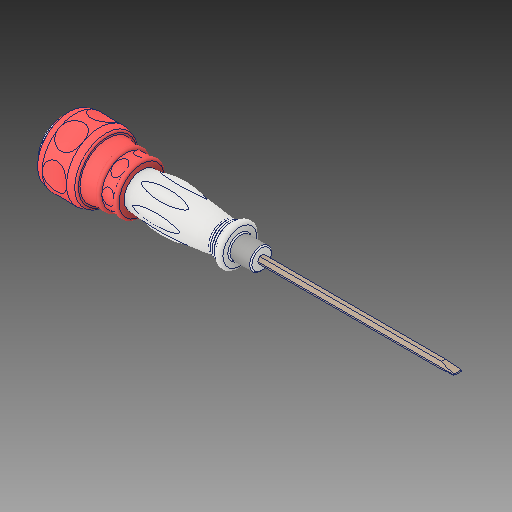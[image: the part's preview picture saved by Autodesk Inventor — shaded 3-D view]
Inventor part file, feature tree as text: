
AUTODESK INVENTOR PART (.ipt)
format: ipt  version: 2018 (Build 220112000, 112)  size: 310,784 bytes
history: native  units: in
note: dims shown in document units (in); Inventor stores cm internally (conversion verified against a paired STEP export)
features: fillet x1
ambient origin geometry x8: Origin, YZ Plane, XZ Plane, XY Plane, X Axis, Y Axis, Z Axis, Center Point
bodies: Solid1 (feature_tree)
feature tree (1):
  fillet  "Fillet3"  [1 undecoded]
note: 1 required parameter value undecoded (feature->parameter linkage not recoverable at this tier; creation-order binding heuristic only, values carry confidence <= 0.55)
